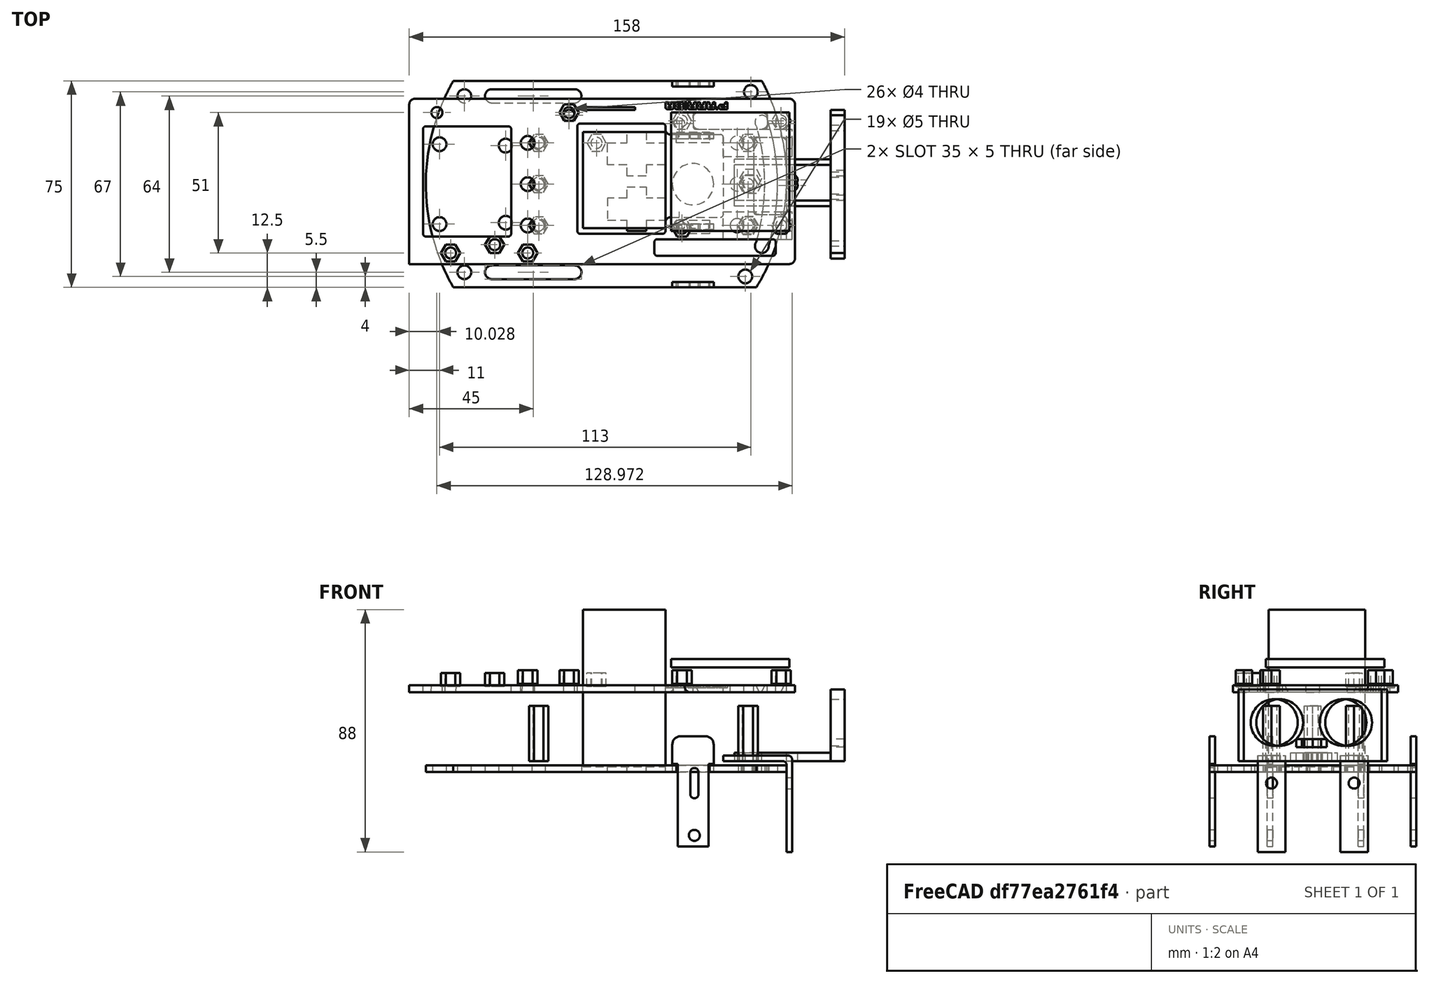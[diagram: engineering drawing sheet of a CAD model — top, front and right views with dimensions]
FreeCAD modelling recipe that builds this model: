
FCSTD DOCUMENT  (FreeCAD 0.17R13541 (Git))
Label: masayloChino2020B
License: All rights reserved
LicenseURL: http://en.wikipedia.org/wiki/All_rights_reserved
objects: Part::Cylinder×48, Part::Cut×40, Part::Box×29, Part::Feature×23, Part::MultiFuse×21, Part::Prism×17, Part::Extrusion×15, Part::Fillet×11, Mesh::Feature×5, Sketcher::SketchObject×1, PartDesign::Pad×1, PartDesign::Body×1, Part::FeaturePython×1
note: 209 computed .brp shape members not serialized (recipe doc carries the construction recipe); baked Part::Feature solids carry a one-line shape summary decoded from their .brp

FEATURE [Sketcher::SketchObject] Sketch
  MapMode = 5
  Support = -> [XY_Plane]
  sketch-geometry (71):
    g0: LineSegment StartX=0 StartY=37.5 StartZ=0 EndX=81 EndY=37.5 EndZ=0
    g1: LineSegment StartX=110 StartY=-37.5 StartZ=0 EndX=93 EndY=-37.5 EndZ=0
    g2: Circle CenterX=4 CenterY=-32 CenterZ=0 NormalX=0 NormalY=0 NormalZ=1 AngleXU=0 Radius=2.5
    g3: ArcOfCircle CenterX=14 CenterY=-32 CenterZ=0 NormalX=0 NormalY=0 NormalZ=1 AngleXU=0 Radius=2.5 StartAngle=1.5708 EndAngle=4.71239
    g4: ArcOfCircle CenterX=44 CenterY=-32 CenterZ=0 NormalX=0 NormalY=0 NormalZ=1 AngleXU=0 Radius=2.5 StartAngle=4.71239 EndAngle=7.85398
    g5: LineSegment StartX=14 StartY=-34.5 StartZ=0 EndX=44 EndY=-34.5 EndZ=0
    g6: LineSegment StartX=14 StartY=-29.5 StartZ=0 EndX=44 EndY=-29.5 EndZ=0
    g7: Circle CenterX=-5 CenterY=-14.5 CenterZ=0 NormalX=0 NormalY=0 NormalZ=1 AngleXU=0 Radius=2.5
    g8: Circle CenterX=-5 CenterY=14.5 CenterZ=0 NormalX=0 NormalY=0 NormalZ=1 AngleXU=0 Radius=2.5
    g9: Circle CenterX=19 CenterY=-14 CenterZ=0 NormalX=0 NormalY=0 NormalZ=1 AngleXU=0 Radius=2.5
    g10: Circle CenterX=31 CenterY=-15 CenterZ=0 NormalX=0 NormalY=0 NormalZ=1 AngleXU=0 Radius=2.5
    g11: ArcOfCircle CenterX=65.3673 CenterY=0 CenterZ=0 NormalX=0 NormalY=0 NormalZ=1 AngleXU=0 Radius=75.36 StartAngle=2.62075 EndAngle=3.66244
    g12: ArcOfCircle CenterX=14 CenterY=32 CenterZ=0 NormalX=0 NormalY=0 NormalZ=1 AngleXU=0 Radius=2.5 StartAngle=1.5708 EndAngle=4.71239
    g13: ArcOfCircle CenterX=44 CenterY=32 CenterZ=0 NormalX=0 NormalY=0 NormalZ=1 AngleXU=0 Radius=2.5 StartAngle=4.71239 EndAngle=7.85398
    g14: LineSegment StartX=14 StartY=29.5 StartZ=0 EndX=44 EndY=29.5 EndZ=0
    g15: LineSegment StartX=14 StartY=34.5 StartZ=0 EndX=44 EndY=34.5 EndZ=0
    g16: Circle CenterX=4 CenterY=32 CenterZ=0 NormalX=0 NormalY=0 NormalZ=1 AngleXU=0 Radius=2.5
    g17: Circle CenterX=31 CenterY=0 CenterZ=0 NormalX=0 NormalY=0 NormalZ=1 AngleXU=0 Radius=2.5
    g18: Circle CenterX=31 CenterY=15 CenterZ=0 NormalX=0 NormalY=0 NormalZ=1 AngleXU=0 Radius=2.5
    g19: LineSegment StartX=56 StartY=-13 StartZ=0 EndX=63 EndY=-13 EndZ=0
    g20: LineSegment StartX=77 StartY=-13 StartZ=0 EndX=77 EndY=-5 EndZ=0
    g21: LineSegment StartX=77 StartY=-5 StartZ=0 EndX=70 EndY=-5 EndZ=0
    g22: LineSegment StartX=56 StartY=-5 StartZ=0 EndX=56 EndY=-13 EndZ=0
    g23: LineSegment StartX=63 StartY=-1 StartZ=0 EndX=70 EndY=-1 EndZ=0
    g24: LineSegment StartX=70 StartY=-1 StartZ=0 EndX=70 EndY=-5 EndZ=0
    g25: LineSegment StartX=70 StartY=-17 StartZ=0 EndX=63 EndY=-17 EndZ=0
    g26: LineSegment StartX=63 StartY=-17 StartZ=0 EndX=63 EndY=-13 EndZ=0
    g27: LineSegment StartX=63 StartY=-5 StartZ=0 EndX=56 EndY=-5 EndZ=0
    g28: LineSegment StartX=63 StartY=-5 StartZ=0 EndX=63 EndY=-1 EndZ=0
    g29: LineSegment StartX=70 StartY=-13 StartZ=0 EndX=70 EndY=-17 EndZ=0
    g30: LineSegment StartX=70 StartY=-13 StartZ=0 EndX=77 EndY=-13 EndZ=0
    g31: Circle CenterX=87 CenterY=0 CenterZ=0 NormalX=0 NormalY=0 NormalZ=1 AngleXU=0 Radius=7.5
    g32: LineSegment StartX=63 StartY=19 StartZ=0 EndX=70 EndY=19 EndZ=0
    g33: LineSegment StartX=70 StartY=19 StartZ=0 EndX=70 EndY=15 EndZ=0
    g34: LineSegment StartX=70 StartY=3 StartZ=0 EndX=63 EndY=3 EndZ=0
    g35: LineSegment StartX=63 StartY=3 StartZ=0 EndX=63 EndY=7 EndZ=0
    g36: LineSegment StartX=56 StartY=15 StartZ=0 EndX=63 EndY=15 EndZ=0
    g37: LineSegment StartX=77 StartY=15 StartZ=0 EndX=77 EndY=7 EndZ=0
    g38: LineSegment StartX=77 StartY=7 StartZ=0 EndX=70 EndY=7 EndZ=0
    g39: LineSegment StartX=56 StartY=7 StartZ=0 EndX=56 EndY=15 EndZ=0
    g40: LineSegment StartX=63 StartY=15 StartZ=0 EndX=63 EndY=19 EndZ=0
    g41: LineSegment StartX=70 StartY=7 StartZ=0 EndX=70 EndY=3 EndZ=0
    g42: LineSegment StartX=63 StartY=7 StartZ=0 EndX=56 EndY=7 EndZ=0
    g43: LineSegment StartX=70 StartY=15 StartZ=0 EndX=77 EndY=15 EndZ=0
    g44: LineSegment StartX=81 StartY=-13 StartZ=0 EndX=93 EndY=-13 EndZ=0
    g45: LineSegment StartX=93 StartY=-13 StartZ=0 EndX=93 EndY=-18 EndZ=0
    g46: LineSegment StartX=93 StartY=-18 StartZ=0 EndX=81 EndY=-18 EndZ=0
    g47: LineSegment StartX=81 StartY=-18 StartZ=0 EndX=81 EndY=-13 EndZ=0
    g48: LineSegment StartX=81 StartY=19 StartZ=0 EndX=93 EndY=19 EndZ=0
    g49: LineSegment StartX=93 StartY=19 StartZ=0 EndX=93 EndY=15 EndZ=0
    g50: LineSegment StartX=93 StartY=15 StartZ=0 EndX=81 EndY=15 EndZ=0
    g51: LineSegment StartX=81 StartY=15 StartZ=0 EndX=81 EndY=19 EndZ=0
    g52: Circle CenterX=107 CenterY=0 CenterZ=0 NormalX=0 NormalY=0 NormalZ=1 AngleXU=0 Radius=2
    g53: Circle CenterX=107 CenterY=-15 CenterZ=0 NormalX=0 NormalY=0 NormalZ=1 AngleXU=0 Radius=2.5
    g54: Circle CenterX=107 CenterY=15 CenterZ=0 NormalX=0 NormalY=0 NormalZ=1 AngleXU=0 Radius=2.5
    g55: Circle CenterX=106 CenterY=-33.5 CenterZ=0 NormalX=0 NormalY=0 NormalZ=1 AngleXU=0 Radius=2.5
    g56: Circle CenterX=108 CenterY=33.5 CenterZ=0 NormalX=0 NormalY=0 NormalZ=1 AngleXU=0 Radius=2.5
    g57: ArcOfCircle CenterX=45.6636 CenterY=1.7423 CenterZ=0 NormalX=0 NormalY=0 NormalZ=1 AngleXU=0 Radius=75.36 StartAngle=5.73548 EndAngle=6.77757
    g58: ArcOfCircle CenterX=112 CenterY=22.5 CenterZ=0 NormalX=0 NormalY=0 NormalZ=1 AngleXU=0 Radius=2.5 StartAngle=0.75994 EndAngle=3.89869
    g59: ArcOfCircle CenterX=112 CenterY=-22.5 CenterZ=0 NormalX=0 NormalY=0 NormalZ=1 AngleXU=0 Radius=2.5 StartAngle=2.5229 EndAngle=6.37272
    g60: ArcOfCircle CenterX=39.6948 CenterY=-0.112448 CenterZ=0 NormalX=0 NormalY=0 NormalZ=1 AngleXU=0 Radius=78.01 StartAngle=5.9951 EndAngle=6.60042
    g61: ArcOfCircle CenterX=38.1627 CenterY=0.243776 CenterZ=0 NormalX=0 NormalY=0 NormalZ=1 AngleXU=0 Radius=74.8917 StartAngle=5.99488 EndAngle=6.561
    g62: LineSegment StartX=81 StartY=-35.5 StartZ=0 EndX=93 EndY=-35.5 EndZ=0
    g63: LineSegment StartX=93 StartY=-35.5 StartZ=0 EndX=93 EndY=-37.5 EndZ=0
    g64: LineSegment StartX=81 StartY=-37.5 StartZ=0 EndX=81 EndY=-35.5 EndZ=0
    g65: LineSegment StartX=81 StartY=-37.5 StartZ=0 EndX=0 EndY=-37.5 EndZ=0
    g66: LineSegment StartX=93 StartY=37.5 StartZ=0 EndX=93 EndY=35.5 EndZ=0
    g67: LineSegment StartX=93 StartY=35.5 StartZ=0 EndX=81 EndY=35.5 EndZ=0
    g68: LineSegment StartX=81 StartY=35.5 StartZ=0 EndX=81 EndY=37.5 EndZ=0
    g69: LineSegment StartX=93 StartY=37.5 StartZ=0 EndX=112 EndY=37.5 EndZ=0
    g70: Circle CenterX=19 CenterY=14 CenterZ=0 NormalX=0 NormalY=0 NormalZ=1 AngleXU=0 Radius=2.5
  constraints (200):
    c: Horizontal(g0)
    c: Horizontal(g1)
    c: DistanceX(g65,g1) = 110
    c: DistanceY(g1,g69) = 75
    c: PointOnObject(g0,g-2)
    c: Radius(g2) = 2.5
    c: DistanceY(g65,g2) = 5.5
    c: DistanceX(g2) = 4
    c: Tangent(g3,g6) = 1.5708
    c: Tangent(g3,g5) = -1.5708
    c: Tangent(g5,g4) = -1.5708
    c: Tangent(g6,g4) = 1.5708
    c: Horizontal(g5)
    c: Equal(g3,g4)
    c: Radius(g3) = 2.5
    c: DistanceY(g65,g3) = 5.5
    c: DistanceX(g3,g4) = 30
    c: DistanceX(g2,g3) = 10
    c: Radius(g7) = 2.5
    c: DistanceY(g65,g7) = 23
    c: DistanceX(g7,g65) = 5
    c: Radius(g8) = 2.5
    c: DistanceY(g8,g0) = 23
    c: DistanceX(g8,g0) = 5
    c: Radius(g9) = 2.5
    c: DistanceY(g2,g9) = 18
    c: DistanceX(g2,g9) = 15
    c: Radius(g10) = 2.5
    c: DistanceX(g9,g10) = 12
    c: DistanceY(g3,g10) = 17
    c: DistanceY(g65,g-1) = 37.5
    c: Coincident(g11,g65)
    c: Radius(g11) = 75.36
    c: Coincident(g11,g0)
    c: PointOnObject(g65,g-2)
    c: Tangent(g12,g15) = 1.5708
    c: Tangent(g12,g14) = -1.5708
    c: Tangent(g14,g13) = -1.5708
    c: Tangent(g15,g13) = 1.5708
    c: Horizontal(g14)
    c: Equal(g12,g13)
    c: Radius(g13) = 2.5
    c: DistanceX(g12,g13) = 30
    c: Radius(g16) = 2.5
    c: DistanceX(g0,g16) = 4
    c: DistanceY(g16,g0) = 5.5
    c: DistanceY(g12,g0) = 5.5
    c: DistanceX(g16,g12) = 10
    c: Radius(g18) = 2.5
    c: Radius(g17) = 2.5
    c: DistanceX(g9,g17) = 12
    c: DistanceY(g10,g17) = 15
    c: DistanceX(g9,g18) = 12
    c: DistanceY(g17,g18) = 15
    c: Coincident(g30,g20)
    c: Coincident(g20,g21)
    c: Coincident(g27,g22)
    c: Coincident(g22,g19)
    c: Horizontal(g19)
    c: Horizontal(g21)
    c: Vertical(g20)
    c: Vertical(g22)
    c: DistanceX(g4,g27) = 12
    c: DistanceX(g27,g20) = 21
    c: DistanceY(g20,g20) = 8
    c: DistanceY(g4,g19) = 19
    c: Coincident(g23,g24)
    c: Coincident(g29,g25)
    c: Coincident(g25,g26)
    c: Coincident(g28,g23)
    c: Horizontal(g23)
    c: Horizontal(g25)
    c: Vertical(g24)
    c: Vertical(g26)
    c: DistanceX(g19,g25) = 7
    c: DistanceY(g25,g19) = 4
    c: DistanceY(g27,g23) = 4
    c: DistanceX(g23,g23) = 7
    c: Tangent(g21,g27)
    c: Coincident(g28,g27)
    c: Tangent(g26,g28)
    c: Coincident(g24,g21)
    c: Tangent(g24,g29)
    c: Coincident(g19,g26)
    c: Coincident(g30,g29)
    c: Tangent(g19,g30)
    c: Radius(g31) = 7.5
    c: PointOnObject(g31,g-1)
    c: DistanceX(g20,g31) = 10
    c: Coincident(g32,g33)
    c: Coincident(g41,g34)
    c: Coincident(g34,g35)
    c: Coincident(g40,g32)
    c: Horizontal(g32)
    c: Horizontal(g34)
    c: Vertical(g33)
    c: Vertical(g35)
    c: Coincident(g43,g37)
    c: Coincident(g37,g38)
    c: Coincident(g42,g39)
    c: Coincident(g39,g36)
    c: Horizontal(g36)
    c: Horizontal(g38)
    c: Vertical(g37)
    c: Vertical(g39)
    c: Tangent(g35,g40)
    c: Tangent(g33,g41)
    c: Coincident(g38,g41)
    c: Coincident(g42,g35)
    c: Tangent(g38,g42)
    c: Coincident(g36,g40)
    c: Coincident(g43,g33)
    c: Tangent(g36,g43)
    c: DistanceX(g42,g42) = 7
    c: DistanceY(g35,g35) = 4
    c: DistanceX(g34,g23) = 0
    c: DistanceY(g23,g34) = 4
    c: DistanceX(g34,g23) = 0
    c: DistanceX(g38,g38) = 7
    c: DistanceY(g37,g37) = 8
    c: DistanceY(g33,g32) = 4
    c: Coincident(g44,g45)
    c: Coincident(g45,g46)
    c: Coincident(g46,g47)
    c: Coincident(g47,g44)
    c: Horizontal(g44)
    c: Horizontal(g46)
    c: Vertical(g45)
    c: Vertical(g47)
    c: DistanceX(g46,g46) = 12
    c: DistanceY(g45,g45) = 5
    c: DistanceX(g20,g44) = 4
    c: DistanceY(g20,g44) = 0
    c: Coincident(g48,g49)
    c: Coincident(g49,g50)
    c: Coincident(g50,g51)
    c: Coincident(g51,g48)
    c: Horizontal(g48)
    c: Horizontal(g50)
    c: Vertical(g49)
    c: Vertical(g51)
    c: DistanceX(g50,g50) = 12
    c: DistanceY(g49,g49) = 4
    c: DistanceY(g37,g50) = 0
    c: DistanceX(g37,g50) = 4
    c: PointOnObject(g52,g-1)
    c: Radius(g52) = 2
    c: DistanceX(g31,g52) = 20
    c: Radius(g53) = 2.5
    c: Radius(g54) = 2.5
    c: DistanceX(g53,g52) = 0
    c: DistanceX(g54,g52) = 0
    c: DistanceY(g52,g54) = 15
    c: DistanceY(g53,g52) = 15
    c: Radius(g55) = 2.5
    c: DistanceX(g55,g1) = 4
    c: DistanceY(g1,g55) = 4
    c: Radius(g56) = 2.5
    c: DistanceX(g56,g69) = 4
    c: DistanceY(g56,g69) = 4
    c: Coincident(g57,g69)
    c: Coincident(g57,g1)
    c: DistanceX(g0,g69) = 112
    c: Radius(g57) = 75.36
    c: Radius(g59) = 2.5
    c: Radius(g58) = 2.5
    c: DistanceY(g54,g58) = 7.5
    c: DistanceX(g54,g58) = 5
    c: DistanceY(g59,g53) = 7.5
    c: DistanceX(g53,g59) = 5
    c: Coincident(g58,g60)
    c: Coincident(g58,g61)
    c: Coincident(g59,g61)
    c: Coincident(g59,g60)
    c: Coincident(g62,g63)
    c: Coincident(g64,g62)
    c: Horizontal(g62)
    c: Vertical(g63)
    c: Vertical(g64)
    c: DistanceX(g62,g46) = 0
    c: DistanceX(g45,g62) = 0
    c: DistanceY(g64,g62) = 2
    c: Coincident(g1,g63)
    c: PointOnObject(g65,g64)
    c: Tangent(g1,g65)
    c: Coincident(g66,g67)
    c: Coincident(g67,g68)
    c: Horizontal(g67)
    c: Vertical(g66)
    c: Vertical(g68)
    c: PointOnObject(g66,g0)
    c: DistanceY(g66,g66) = 2
    c: DistanceX(g48,g66) = 0
    c: DistanceX(g67,g48) = 0
    c: PointOnObject(g0,g68)
    c: PointOnObject(g69,g66)
    c: Tangent(g0,g69)
    c: Radius(g70) = 2.5
    c: DistanceX(g70,g18) = 12
    c: DistanceY(g70,g18) = 1
FEATURE [PartDesign::Pad] Pad
  Length = 2.5
  Length2 = 100
  Profile = -> Sketch
  Type = 0
FEATURE [PartDesign::Body] Body
  Group = -> [Sketch,Pad]
  Origin = -> Origin
  Tip = -> Pad
FEATURE [Part::Box] Box  label="Cubo"
  AttacherType = Attacher::AttachEngine3D
  Height = 2.5
  Length = 140
  Placement = pos=(10,-31,25) rot=(0,0,1;0rad)
  Width = 60
FEATURE [Part::Cylinder] Cylinder  label="Cilindro"
  Angle = 360
  AttacherType = Attacher::AttachEngine3D
  Height = 50
  Placement = pos=(31,0,-4) rot=(0,0,1;0rad)
  Radius = 2.5
FEATURE [Part::Cylinder] Cylinder001  label="Cilindro001"
  Angle = 360
  AttacherType = Attacher::AttachEngine3D
  Height = 50
  Placement = pos=(31,-15,-4) rot=(0,0,1;0rad)
  Radius = 2.5
FEATURE [Part::Cylinder] Cylinder002  label="Cilindro002"
  Angle = 360
  AttacherType = Attacher::AttachEngine3D
  Height = 50
  Placement = pos=(31,15,-4) rot=(0,0,1;0rad)
  Radius = 2.5
FEATURE [Part::Cylinder] Cylinder003  label="Cilindro003"
  Angle = 360
  AttacherType = Attacher::AttachEngine3D
  Height = 50
  Placement = pos=(107,15,-4) rot=(0,0,1;0rad)
  Radius = 2.5
FEATURE [Part::Cylinder] Cylinder004  label="Cilindro004"
  Angle = 360
  AttacherType = Attacher::AttachEngine3D
  Height = 50
  Placement = pos=(107,0,-4) rot=(0,0,1;0rad)
  Radius = 2.5
FEATURE [Part::Cylinder] Cylinder005  label="Cilindro005"
  Angle = 360
  AttacherType = Attacher::AttachEngine3D
  Height = 50
  Placement = pos=(107,-15,-4) rot=(0,0,1;0rad)
  Radius = 2.5
FEATURE [Part::MultiFuse] Fusion
  Shapes = -> [Cylinder,Cylinder001,Cylinder002,Cylinder003,Cylinder004,Cylinder005]
FEATURE [Part::Cut] Cut
  Base = -> Box
  Tool = -> Fusion
FEATURE [Part::Cylinder] Cylinder006  label="Cilindro006"
  Angle = 360
  AttacherType = Attacher::AttachEngine3D
  Height = 10
  Placement = pos=(3,3,47) rot=(0,0,1;0rad)
  Radius = 2
FEATURE [Part::Cylinder] Cylinder007  label="Cilindro007"
  Angle = 360
  AttacherType = Attacher::AttachEngine3D
  Height = 10
  Placement = pos=(3,40,47) rot=(0,0,1;0rad)
  Radius = 2
FEATURE [Part::Cylinder] Cylinder008  label="Cilindro008"
  Angle = 360
  AttacherType = Attacher::AttachEngine3D
  Height = 10
  Placement = pos=(40,3,47) rot=(0,0,1;0rad)
  Radius = 2
FEATURE [Part::Cylinder] Cylinder009  label="Cilindro009"
  Angle = 360
  AttacherType = Attacher::AttachEngine3D
  Height = 10
  Placement = pos=(40,40,47) rot=(0,0,1;0rad)
  Radius = 2
FEATURE [Part::Box] Box001  label="l298n"
  AttacherType = Attacher::AttachEngine3D
  Height = 3
  Length = 43
  Placement = pos=(79,-17,38) rot=(0,0,1;0rad)
  Width = 43
FEATURE [Part::MultiFuse] Fusion001  label="TALADROSL298N"
  Placement = pos=(12,-25,-27) rot=(0,0,1;0rad)
  Shapes = -> [Cylinder006,Cylinder007,Cylinder009,Cylinder008]
FEATURE [Part::Cylinder] Cylinder010  label="Cilindro010"
  Angle = 360
  AttacherType = Attacher::AttachEngine3D
  Height = 10
  Placement = pos=(31,-16,-2) rot=(0,0,1;0rad)
  Radius = 2
FEATURE [Part::Cylinder] Cylinder011  label="Cilindro011"
  Angle = 360
  AttacherType = Attacher::AttachEngine3D
  Height = 10
  Placement = pos=(79,-17,-2) rot=(0,0,1;0rad)
  Radius = 2
FEATURE [Part::Cylinder] Cylinder012  label="Cilindro012"
  Angle = 360
  AttacherType = Attacher::AttachEngine3D
  Height = 10
  Placement = pos=(74,34,-2) rot=(0,0,1;0rad)
  Radius = 2
FEATURE [Part::Cylinder] Cylinder013  label="Cilindro013"
  Angle = 360
  AttacherType = Attacher::AttachEngine3D
  Height = 10
  Placement = pos=(46,34,-2) rot=(0,0,1;0rad)
  Radius = 2
FEATURE [Part::MultiFuse] Fusion002  label="taladrosNanoShield"
  Placement = pos=(61,-9,24) rot=(0,-1,0;0.017453rad)
  Shapes = -> [Cylinder013,Cylinder011,Cylinder010,Cylinder012]
FEATURE [Part::MultiFuse] Fusion003  label="TALADROSPISO2"
  Shapes = -> [Fusion001,Fusion002]
FEATURE [Part::Cut] Cut001
  Base = -> Cut
  Tool = -> Fusion003
FEATURE [Part::Box] Box002  label="Cubo001"
  AttacherType = Attacher::AttachEngine3D
  Height = 10
  Length = 52
  Placement = pos=(36,-18,20) rot=(0,0,1;0rad)
  Width = 30
FEATURE [Part::Box] Box003  label="Cubo002"
  AttacherType = Attacher::AttachEngine3D
  Height = 10
  Length = 19
  Placement = pos=(68,-28,20) rot=(0,0,1;0rad)
  Width = 1
FEATURE [Part::Box] Box004  label="Cubo003"
  AttacherType = Attacher::AttachEngine3D
  Height = 10
  Length = 12
  Placement = pos=(13,-17,20) rot=(0,0,1;0rad)
  Width = 28
FEATURE [Part::Box] Box005  label="Cubo004"
  AttacherType = Attacher::AttachEngine3D
  Height = 10
  Length = 44
  Placement = pos=(17,20,20) rot=(0,0,1;0rad)
  Width = 6
FEATURE [Part::Box] Box006  label="Cubo005"
  AttacherType = Attacher::AttachEngine3D
  Height = 10
  Length = 27
  Placement = pos=(20,-26,20) rot=(0,0,1;0rad)
  Width = 6
FEATURE [Part::MultiFuse] Fusion004  label="agujerosPiso2"
  Shapes = -> [Box002,Box003,Box004,Box005,Box006]
FEATURE [Part::Cut] Cut002
  Base = -> Cut001
  Tool = -> Fusion004
FEATURE [Part::Fillet] Fillet  label="piso2"
  Base = -> Cut002
  Edges = 4 edges r=2: [Edge1,Edge3,Edge6,Edge47]
  Placement = pos=(0,0,4) rot=(0,0,1;0rad)
FEATURE [Part::Cylinder] Cylinder014  label="Cilindro014"
  Angle = 360
  AttacherType = Attacher::AttachEngine3D
  Height = 30
  Placement = pos=(0,0,-2) rot=(0,0,1;0rad)
  Radius = 2
FEATURE [Part::Prism] Prism  label="Prisma"
  AttacherType = Attacher::AttachEngine3D
  Circumradius = 3.5
  Height = 20
  Polygon = 6
FEATURE [Part::Cut] Cut003  label="separador"
  Base = -> Prism
  Placement = pos=(31,0,4) rot=(0,0,1;0rad)
  Tool = -> Cylinder014
FEATURE [Part::Cylinder] Cylinder015  label="Cilindro015"
  Angle = 360
  AttacherType = Attacher::AttachEngine3D
  Height = 30
  Placement = pos=(0,0,-2) rot=(0,0,1;0rad)
  Radius = 2
FEATURE [Part::Prism] Prism001  label="Prisma001"
  AttacherType = Attacher::AttachEngine3D
  Circumradius = 3.5
  Height = 20
  Polygon = 6
FEATURE [Part::Cut] Cut004  label="separador001"
  Base = -> Prism001
  Placement = pos=(31,15,4) rot=(0,0,1;0rad)
  Tool = -> Cylinder015
FEATURE [Part::Cylinder] Cylinder016  label="Cilindro016"
  Angle = 360
  AttacherType = Attacher::AttachEngine3D
  Height = 30
  Placement = pos=(0,0,-2) rot=(0,0,1;0rad)
  Radius = 2
FEATURE [Part::Prism] Prism002  label="Prisma002"
  AttacherType = Attacher::AttachEngine3D
  Circumradius = 3.5
  Height = 20
  Polygon = 6
FEATURE [Part::Cut] Cut005  label="separador002"
  Base = -> Prism002
  Placement = pos=(31,-15,4) rot=(0,0,1;0rad)
  Tool = -> Cylinder016
FEATURE [Part::Prism] Prism003  label="Prisma003"
  AttacherType = Attacher::AttachEngine3D
  Circumradius = 3.5
  Height = 20
  Polygon = 6
FEATURE [Part::Cylinder] Cylinder017  label="Cilindro017"
  Angle = 360
  AttacherType = Attacher::AttachEngine3D
  Height = 30
  Placement = pos=(0,0,-2) rot=(0,0,1;0rad)
  Radius = 2
FEATURE [Part::Cut] Cut006  label="separador003"
  Base = -> Prism003
  Placement = pos=(107,-15,4) rot=(0,0,1;0rad)
  Tool = -> Cylinder017
FEATURE [Part::Cylinder] Cylinder018  label="Cilindro018"
  Angle = 360
  AttacherType = Attacher::AttachEngine3D
  Height = 30
  Placement = pos=(0,0,-2) rot=(0,0,1;0rad)
  Radius = 2
FEATURE [Part::Prism] Prism004  label="Prisma004"
  AttacherType = Attacher::AttachEngine3D
  Circumradius = 3.5
  Height = 20
  Polygon = 6
FEATURE [Part::Cut] Cut007  label="separador004"
  Base = -> Prism004
  Placement = pos=(107,0,4) rot=(0,0,1;0rad)
  Tool = -> Cylinder018
FEATURE [Part::Cylinder] Cylinder019  label="Cilindro019"
  Angle = 360
  AttacherType = Attacher::AttachEngine3D
  Height = 30
  Placement = pos=(0,0,-2) rot=(0,0,1;0rad)
  Radius = 2
FEATURE [Part::Prism] Prism005  label="Prisma005"
  AttacherType = Attacher::AttachEngine3D
  Circumradius = 3.5
  Height = 20
  Polygon = 6
FEATURE [Part::Cut] Cut008  label="separador005"
  Base = -> Prism005
  Placement = pos=(107,15,4) rot=(0,0,1;0rad)
  Tool = -> Cylinder019
FEATURE [Part::Box] Box007  label="Cubo006"
  AttacherType = Attacher::AttachEngine3D
  Height = 33
  Length = 11.2
  Placement = pos=(81.5,35.5,-27) rot=(0,0,1;0rad)
  Width = 2
FEATURE [Part::Cylinder] Cylinder022  label="Cilindro022"
  Angle = 360
  AttacherType = Attacher::AttachEngine3D
  Height = 10
  Placement = pos=(87.5,41.5,-8) rot=(1,0,0;1.5708rad)
  Radius = 1.5
FEATURE [Part::Box] Box009  label="Cubo008"
  AttacherType = Attacher::AttachEngine3D
  Height = 8
  Length = 3
  Placement = pos=(86,32,-8) rot=(0,0,1;0rad)
  Width = 10
FEATURE [Part::Cylinder] Cylinder021  label="Cilindro021"
  Angle = 360
  AttacherType = Attacher::AttachEngine3D
  Height = 10
  Placement = pos=(87.5,41.5,0) rot=(1,0,0;1.5708rad)
  Radius = 1.5
FEATURE [Part::Cylinder] Cylinder023  label="Cilindro023"
  Angle = 360
  AttacherType = Attacher::AttachEngine3D
  Height = 10
  Placement = pos=(87.5,41.5,-23) rot=(1,0,0;1.5708rad)
  Radius = 2
FEATURE [Part::MultiFuse] Fusion006
  Shapes = -> [Box009,Cylinder022,Cylinder021,Cylinder023]
FEATURE [Part::Box] Box008  label="Cubo007"
  AttacherType = Attacher::AttachEngine3D
  Height = 10
  Length = 15
  Placement = pos=(79.5,35.5,3) rot=(0,0,1;0rad)
  Width = 2
FEATURE [Part::MultiFuse] Fusion005
  Shapes = -> [Box007,Box008]
FEATURE [Part::Fillet] Fillet001
  Base = -> Fusion005
  Edges = 2 edges r=3: [Edge30,Edge32]
FEATURE [Part::Cut] Cut010  label="colocador"
  Base = -> Fillet001
  Tool = -> Fusion006
FEATURE [Part::Box] Box010  label="Cubo009"
  AttacherType = Attacher::AttachEngine3D
  Height = 33
  Length = 11.2
  Placement = pos=(81.5,35.5,-27) rot=(0,0,1;0rad)
  Width = 2
FEATURE [Part::Cylinder] Cylinder024  label="Cilindro024"
  Angle = 360
  AttacherType = Attacher::AttachEngine3D
  Height = 10
  Placement = pos=(87.5,41.5,0) rot=(1,0,0;1.5708rad)
  Radius = 1.5
FEATURE [Part::Box] Box011  label="Cubo010"
  AttacherType = Attacher::AttachEngine3D
  Height = 10
  Length = 15
  Placement = pos=(79.5,35.5,3) rot=(0,0,1;0rad)
  Width = 2
FEATURE [Part::MultiFuse] Fusion007
  Shapes = -> [Box010,Box011]
FEATURE [Part::Fillet] Fillet002
  Base = -> Fusion007
  Edges = 2 edges r=3: [Edge30,Edge32]
FEATURE [Part::Cylinder] Cylinder025  label="Cilindro025"
  Angle = 360
  AttacherType = Attacher::AttachEngine3D
  Height = 10
  Placement = pos=(87.5,41.5,-8) rot=(1,0,0;1.5708rad)
  Radius = 1.5
FEATURE [Part::Cylinder] Cylinder026  label="Cilindro026"
  Angle = 360
  AttacherType = Attacher::AttachEngine3D
  Height = 10
  Placement = pos=(87.5,41.5,-23) rot=(1,0,0;1.5708rad)
  Radius = 2
FEATURE [Part::Box] Box012  label="Cubo011"
  AttacherType = Attacher::AttachEngine3D
  Height = 8
  Length = 3
  Placement = pos=(86,32,-8) rot=(0,0,1;0rad)
  Width = 10
FEATURE [Part::MultiFuse] Fusion008
  Shapes = -> [Box012,Cylinder025,Cylinder024,Cylinder026]
FEATURE [Part::Cut] Cut011  label="colocador001"
  Base = -> Fillet002
  Placement = pos=(0,-19,0) rot=(0,0,1;0rad)
  Tool = -> Fusion008
FEATURE [Part::Box] Box013  label="Cubo012"
  AttacherType = Attacher::AttachEngine3D
  Height = 33
  Length = 11.2
  Placement = pos=(81.5,35.5,-27) rot=(0,0,1;0rad)
  Width = 2
FEATURE [Part::Cylinder] Cylinder027  label="Cilindro027"
  Angle = 360
  AttacherType = Attacher::AttachEngine3D
  Height = 10
  Placement = pos=(87.5,41.5,0) rot=(1,0,0;1.5708rad)
  Radius = 1.5
FEATURE [Part::Box] Box014  label="Cubo013"
  AttacherType = Attacher::AttachEngine3D
  Height = 10
  Length = 15
  Placement = pos=(79.5,35.5,3) rot=(0,0,1;0rad)
  Width = 2
FEATURE [Part::MultiFuse] Fusion009
  Shapes = -> [Box013,Box014]
FEATURE [Part::Fillet] Fillet003
  Base = -> Fusion009
  Edges = 2 edges r=3: [Edge30,Edge32]
FEATURE [Part::Cylinder] Cylinder028  label="Cilindro028"
  Angle = 360
  AttacherType = Attacher::AttachEngine3D
  Height = 10
  Placement = pos=(87.5,41.5,-8) rot=(1,0,0;1.5708rad)
  Radius = 1.5
FEATURE [Part::Cylinder] Cylinder029  label="Cilindro029"
  Angle = 360
  AttacherType = Attacher::AttachEngine3D
  Height = 10
  Placement = pos=(87.5,41.5,-23) rot=(1,0,0;1.5708rad)
  Radius = 2
FEATURE [Part::Box] Box015  label="Cubo014"
  AttacherType = Attacher::AttachEngine3D
  Height = 8
  Length = 3
  Placement = pos=(86,32,-8) rot=(0,0,1;0rad)
  Width = 10
FEATURE [Part::MultiFuse] Fusion010
  Shapes = -> [Box015,Cylinder028,Cylinder027,Cylinder029]
FEATURE [Part::Cut] Cut012  label="colocador002"
  Base = -> Fillet003
  Placement = pos=(0,-52,0) rot=(0,0,1;0rad)
  Tool = -> Fusion010
FEATURE [Part::Cylinder] Cylinder030  label="Cilindro030"
  Angle = 360
  AttacherType = Attacher::AttachEngine3D
  Height = 10
  Placement = pos=(87.5,41.5,-8) rot=(1,0,0;1.5708rad)
  Radius = 1.5
FEATURE [Part::Box] Box016  label="Cubo015"
  AttacherType = Attacher::AttachEngine3D
  Height = 8
  Length = 3
  Placement = pos=(86,32,-8) rot=(0,0,1;0rad)
  Width = 10
FEATURE [Part::Box] Box017  label="Cubo016"
  AttacherType = Attacher::AttachEngine3D
  Height = 33
  Length = 11.2
  Placement = pos=(81.5,35.5,-27) rot=(0,0,1;0rad)
  Width = 2
FEATURE [Part::Box] Box018  label="Cubo017"
  AttacherType = Attacher::AttachEngine3D
  Height = 10
  Length = 15
  Placement = pos=(79.5,35.5,3) rot=(0,0,1;0rad)
  Width = 2
FEATURE [Part::Cylinder] Cylinder031  label="Cilindro031"
  Angle = 360
  AttacherType = Attacher::AttachEngine3D
  Height = 10
  Placement = pos=(87.5,41.5,-23) rot=(1,0,0;1.5708rad)
  Radius = 2
FEATURE [Part::Cylinder] Cylinder032  label="Cilindro032"
  Angle = 360
  AttacherType = Attacher::AttachEngine3D
  Height = 10
  Placement = pos=(87.5,41.5,0) rot=(1,0,0;1.5708rad)
  Radius = 1.5
FEATURE [Part::MultiFuse] Fusion011
  Shapes = -> [Box017,Box018]
FEATURE [Part::Fillet] Fillet004
  Base = -> Fusion011
  Edges = 2 edges r=3: [Edge30,Edge32]
FEATURE [Part::MultiFuse] Fusion012
  Shapes = -> [Box016,Cylinder030,Cylinder032,Cylinder031]
FEATURE [Part::Cut] Cut013  label="colocador003"
  Base = -> Fillet004
  Placement = pos=(0,-73,0) rot=(0,0,1;0rad)
  Tool = -> Fusion012
FEATURE [Part::Feature] Cut010_solid  label="colocador (Solid)"
  shape: bbox 15 x 2 x 40 mm, 21 faces (baked)
FEATURE [Mesh::Feature] Mesh002  label="colocador (Solid) (Meshed)"
FEATURE [Part::Cylinder] Cylinder033  label="Cilindro033"
  Angle = 360
  AttacherType = Attacher::AttachEngine3D
  Height = 30
  Placement = pos=(0,0,-2) rot=(0,0,1;0rad)
  Radius = 2
FEATURE [Part::Prism] Prism007  label="Prisma007"
  AttacherType = Attacher::AttachEngine3D
  Circumradius = 3.5
  Height = 5
  Polygon = 6
FEATURE [Part::Cylinder] Cylinder034  label="Cilindro034"
  Angle = 360
  AttacherType = Attacher::AttachEngine3D
  Height = 30
  Placement = pos=(0,0,-2) rot=(0,0,1;0rad)
  Radius = 2
FEATURE [Part::Prism] Prism008  label="Prisma008"
  AttacherType = Attacher::AttachEngine3D
  Circumradius = 3.5
  Height = 5
  Polygon = 6
FEATURE [Part::Cut] Cut015  label="separador008"
  Base = -> Prism008
  Placement = pos=(27,-25,32) rot=(0,0,1;0rad)
  Tool = -> Cylinder034
FEATURE [Part::Cylinder] Cylinder035  label="Cilindro035"
  Angle = 360
  AttacherType = Attacher::AttachEngine3D
  Height = 30
  Placement = pos=(0,0,-2) rot=(0,0,1;0rad)
  Radius = 2
FEATURE [Part::Prism] Prism009  label="Prisma009"
  AttacherType = Attacher::AttachEngine3D
  Circumradius = 3.5
  Height = 5
  Polygon = 6
FEATURE [Part::Cut] Cut016  label="separador009"
  Base = -> Prism009
  Placement = pos=(42,26,32) rot=(0,0,1;0rad)
  Tool = -> Cylinder035
FEATURE [Part::Prism] Prism010  label="Prisma010"
  AttacherType = Attacher::AttachEngine3D
  Circumradius = 3.5
  Height = 5
  Polygon = 6
FEATURE [Part::Cylinder] Cylinder036  label="Cilindro036"
  Angle = 360
  AttacherType = Attacher::AttachEngine3D
  Height = 30
  Placement = pos=(0,0,-2) rot=(0,0,1;0rad)
  Radius = 2
FEATURE [Part::Cut] Cut017  label="separador010"
  Base = -> Prism010
  Placement = pos=(119,23,32) rot=(0,0,1;0rad)
  Tool = -> Cylinder036
FEATURE [Part::Prism] Prism011  label="Prisma011"
  AttacherType = Attacher::AttachEngine3D
  Circumradius = 3.5
  Height = 5
  Polygon = 6
FEATURE [Part::Cylinder] Cylinder037  label="Cilindro037"
  Angle = 360
  AttacherType = Attacher::AttachEngine3D
  Height = 30
  Placement = pos=(0,0,-2) rot=(0,0,1;0rad)
  Radius = 2
FEATURE [Part::Cut] Cut018  label="separador011"
  Base = -> Prism011
  Placement = pos=(83,23,32) rot=(0,0,1;0rad)
  Tool = -> Cylinder037
FEATURE [Part::Prism] Prism012  label="Prisma012"
  AttacherType = Attacher::AttachEngine3D
  Circumradius = 3.5
  Height = 5
  Polygon = 6
FEATURE [Part::Cylinder] Cylinder038  label="Cilindro038"
  Angle = 360
  AttacherType = Attacher::AttachEngine3D
  Height = 30
  Placement = pos=(0,0,-2) rot=(0,0,1;0rad)
  Radius = 2
FEATURE [Part::Cut] Cut019  label="separador012"
  Base = -> Prism012
  Placement = pos=(52,15,31) rot=(0,0,1;0rad)
  Tool = -> Cylinder038
FEATURE [Part::Cylinder] Cylinder039  label="Cilindro039"
  Angle = 360
  AttacherType = Attacher::AttachEngine3D
  Height = 30
  Placement = pos=(0,0,-2) rot=(0,0,1;0rad)
  Radius = 2
FEATURE [Part::Prism] Prism013  label="Prisma013"
  AttacherType = Attacher::AttachEngine3D
  Circumradius = 3.5
  Height = 5
  Polygon = 6
FEATURE [Part::Cut] Cut020  label="separador013"
  Base = -> Prism013
  Placement = pos=(119,-15,32) rot=(0,0,1;0rad)
  Tool = -> Cylinder039
FEATURE [Part::Prism] Prism014  label="Prisma014"
  AttacherType = Attacher::AttachEngine3D
  Circumradius = 3.5
  Height = 5
  Polygon = 6
FEATURE [Part::Cylinder] Cylinder040  label="Cilindro040"
  Angle = 360
  AttacherType = Attacher::AttachEngine3D
  Height = 30
  Placement = pos=(0,0,-2) rot=(0,0,1;0rad)
  Radius = 2
FEATURE [Part::Cut] Cut021  label="separador014"
  Base = -> Prism014
  Placement = pos=(83,-16,32) rot=(0,0,1;0rad)
  Tool = -> Cylinder040
FEATURE [Part::Feature] Cut021_solid  label="separadorSec"
  shape: bbox 7 x 6.062 x 5 mm, 9 faces (baked)
FEATURE [Part::Feature] path4522
  shape: bbox 6.314 x 4.985 x 2.279e-07 mm, 0 faces, 0 solids (baked)
FEATURE [Part::Feature] path4522001
  shape: bbox 2.322 x 1.012 x 2.279e-07 mm, 0 faces, 0 solids (baked)
FEATURE [Part::Feature] path4524
  shape: bbox 1.403 x 1.446 x 2.279e-07 mm, 0 faces, 0 solids (baked)
FEATURE [Part::Feature] path4526
  shape: bbox 6.076 x 4.985 x 2.279e-07 mm, 0 faces, 0 solids (baked)
FEATURE [Part::Feature] path4526001
  shape: bbox 2.174 x 0.6621 x 2.279e-07 mm, 0 faces, 0 solids (baked)
FEATURE [Part::Feature] path4528
  shape: bbox 6.274 x 4.977 x 2.279e-07 mm, 0 faces, 0 solids (baked)
FEATURE [Part::Feature] path4528001
  shape: bbox 2.371 x 0.6621 x 2.279e-07 mm, 0 faces, 0 solids (baked)
FEATURE [Part::Feature] path4530
  shape: bbox 6.274 x 4.977 x 2.279e-07 mm, 0 faces, 0 solids (baked)
FEATURE [Part::Feature] path4530001
  shape: bbox 2.371 x 0.6621 x 2.279e-07 mm, 0 faces, 0 solids (baked)
FEATURE [Part::Feature] path4532
  shape: bbox 1.956 x 4.977 x 2.279e-07 mm, 0 faces, 0 solids (baked)
FEATURE [Part::Feature] path4534
  shape: bbox 6.373 x 4.992 x 2.279e-07 mm, 0 faces, 0 solids (baked)
FEATURE [Part::Feature] path4534001
  shape: bbox 2.391 x 0.6849 x 2.279e-07 mm, 0 faces, 0 solids (baked)
FEATURE [Part::Feature] path4534002
  shape: bbox 2.391 x 0.6849 x 2.279e-07 mm, 0 faces, 0 solids (baked)
FEATURE [Part::Feature] path4536
  shape: bbox 6.076 x 4.985 x 2.279e-07 mm, 0 faces, 0 solids (baked)
FEATURE [Part::Feature] path4536001
  shape: bbox 2.174 x 0.6621 x 2.279e-07 mm, 0 faces, 0 solids (baked)
FEATURE [Part::Extrusion] Extrude
  Base = -> path4522
  Dir = (0,0,-1)
  DirMode = 2
  FaceMakerClass = Part::FaceMakerBullseye
  LengthFwd = 2
  LengthRev = 0
  Solid = true
  Symmetric = false
FEATURE [Part::Extrusion] Extrude001
  Base = -> path4522001
  Dir = (0,0,1)
  DirMode = 2
  FaceMakerClass = Part::FaceMakerBullseye
  LengthFwd = 2
  LengthRev = 0
  Placement = pos=(0,0,-2) rot=(0,0,1;0rad)
  Solid = true
  Symmetric = false
FEATURE [Part::Extrusion] Extrude002
  Base = -> path4524
  Dir = (0,0,-1)
  DirMode = 2
  FaceMakerClass = Part::FaceMakerBullseye
  LengthFwd = 2
  LengthRev = 0
  Solid = true
  Symmetric = false
FEATURE [Part::Extrusion] Extrude003
  Base = -> path4526
  Dir = (0,0,-1)
  DirMode = 2
  FaceMakerClass = Part::FaceMakerBullseye
  LengthFwd = 2
  LengthRev = 0
  Solid = true
  Symmetric = false
FEATURE [Part::Extrusion] Extrude004
  Base = -> path4526001
  Dir = (0,0,1)
  DirMode = 2
  FaceMakerClass = Part::FaceMakerBullseye
  LengthFwd = 2
  LengthRev = 0
  Placement = pos=(0,0,-2) rot=(0,0,1;0rad)
  Solid = true
  Symmetric = false
FEATURE [Part::Extrusion] Extrude005
  Base = -> path4528
  Dir = (0,0,-1)
  DirMode = 2
  FaceMakerClass = Part::FaceMakerBullseye
  LengthFwd = 2
  LengthRev = 0
  Solid = true
  Symmetric = false
FEATURE [Part::Extrusion] Extrude006
  Base = -> path4528001
  Dir = (0,0,1)
  DirMode = 2
  FaceMakerClass = Part::FaceMakerBullseye
  LengthFwd = 2
  LengthRev = 0
  Placement = pos=(0,0,-2) rot=(0,0,1;0rad)
  Solid = true
  Symmetric = false
FEATURE [Part::Extrusion] Extrude007
  Base = -> path4530
  Dir = (0,0,-1)
  DirMode = 2
  FaceMakerClass = Part::FaceMakerBullseye
  LengthFwd = 2
  LengthRev = 0
  Solid = true
  Symmetric = false
FEATURE [Part::Extrusion] Extrude008
  Base = -> path4530001
  Dir = (0,0,1)
  DirMode = 2
  FaceMakerClass = Part::FaceMakerBullseye
  LengthFwd = 2
  LengthRev = 0
  Placement = pos=(0,0,-2) rot=(0,0,1;0rad)
  Solid = true
  Symmetric = false
FEATURE [Part::Extrusion] Extrude009
  Base = -> path4532
  Dir = (0,0,-1)
  DirMode = 2
  FaceMakerClass = Part::FaceMakerBullseye
  LengthFwd = 2
  LengthRev = 0
  Solid = true
  Symmetric = false
FEATURE [Part::Extrusion] Extrude010
  Base = -> path4534
  Dir = (0,0,-1)
  DirMode = 2
  FaceMakerClass = Part::FaceMakerBullseye
  LengthFwd = 2
  LengthRev = 0
  Solid = true
  Symmetric = false
FEATURE [Part::Extrusion] Extrude011
  Base = -> path4534001
  Dir = (0,0,1)
  DirMode = 2
  FaceMakerClass = Part::FaceMakerBullseye
  LengthFwd = 2
  LengthRev = 0
  Placement = pos=(0,0,-2) rot=(0,0,1;0rad)
  Solid = true
  Symmetric = false
FEATURE [Part::Extrusion] Extrude012
  Base = -> path4534002
  Dir = (0,0,1)
  DirMode = 2
  FaceMakerClass = Part::FaceMakerBullseye
  LengthFwd = 2
  LengthRev = 0
  Placement = pos=(0,0,-2) rot=(0,0,1;0rad)
  Solid = true
  Symmetric = false
FEATURE [Part::Extrusion] Extrude013
  Base = -> path4536
  Dir = (0,0,-1)
  DirMode = 2
  FaceMakerClass = Part::FaceMakerBullseye
  LengthFwd = 2
  LengthRev = 0
  Solid = true
  Symmetric = false
FEATURE [Part::Extrusion] Extrude014
  Base = -> path4536001
  Dir = (0,0,1)
  DirMode = 2
  FaceMakerClass = Part::FaceMakerBullseye
  LengthFwd = 2
  LengthRev = 0
  Placement = pos=(0,0,-2) rot=(0,0,1;0rad)
  Solid = true
  Symmetric = false
FEATURE [Part::Cut] Cut023
  Base = -> Extrude
  Tool = -> Extrude001
FEATURE [Part::Cut] Cut024
  Base = -> Extrude003
  Tool = -> Extrude004
FEATURE [Part::Cut] Cut025
  Base = -> Extrude005
  Tool = -> Extrude006
FEATURE [Part::Cut] Cut026
  Base = -> Extrude007
  Tool = -> Extrude008
FEATURE [Part::MultiFuse] Fusion014
  Shapes = -> [Extrude011,Extrude012]
FEATURE [Part::Cut] Cut027
  Base = -> Extrude010
  Tool = -> Fusion014
FEATURE [Part::Cut] Cut028
  Base = -> Extrude013
  Tool = -> Extrude014
FEATURE [Part::MultiFuse] Fusion015  label="PARRIBA"
  Placement = pos=(0,43,33) rot=(0,0,1;0rad)
  Shapes = -> [Extrude002,Extrude009,Cut023,Cut024,Cut025,Cut026,Cut027,Cut028]
FEATURE [Part::FeaturePython] Scale  # Draft clone (typed FeaturePython)
  Fuse = false
  Objects = -> [Fusion015]
  Placement = pos=(9.32,6.53,31.7) rot=(0,0,1;0rad)
  Scale = (0.5,0.5,0.5)
FEATURE [Part::Box] Box019  label="portaPilasAA"
  AttacherType = Attacher::AttachEngine3D
  Height = 57
  Length = 30
  Placement = pos=(47,-16,2) rot=(0,0,1;0rad)
  Width = 35
FEATURE [Part::Box] Box020  label="Cubo018"
  AttacherType = Attacher::AttachEngine3D
  Height = 30
  Length = 32
  Placement = pos=(57,-22,12) rot=(0,0,1;0rad)
  Width = 40
FEATURE [Part::Cut] Cut029
  Base = -> Fillet
  Tool = -> Box020
FEATURE [Part::Cut] Cut030
  Base = -> Cut029
  Tool = -> Scale
FEATURE [Part::Box] Box021  label="Cubo019"
  AttacherType = Attacher::AttachEngine3D
  Height = 10
  Length = 32
  Placement = pos=(113,-21,24) rot=(0,0,1;0rad)
  Width = 40
FEATURE [Part::Cut] Cut031
  Base = -> Cut030
  Tool = -> Box021
FEATURE [Part::Fillet] Fillet005
  Base = -> Cut031
  Edges = 8 edges: [Edge485 r1=2 r2=1,Edge486 r1=2 r2=1,Edge487 r1=2 r2=1,Edge488 r1=2 r2=1,Edge489 r1=2 r2=1,Edge490 r1=2 r2=1,Edge491 r1=2 r2=1,Edge492 r1=2 r2=1]
FEATURE [Part::Fillet] Fillet006
  Base = -> Fillet005
  Edges = 4 edges r=1: [Edge495,Edge496,Edge498,Edge500]
FEATURE [Part::Fillet] Fillet007
  Base = -> Fillet006
  Edges = 4 edges r=1: [Edge497,Edge498,Edge500,Edge502]
FEATURE [Part::Fillet] Fillet008
  Base = -> Fillet007
  Edges = 6 edges r=1: [Edge495,Edge498,Edge500,Edge502,Edge504,Edge506]
FEATURE [Part::Fillet] Fillet009  label="segundoPiso"
  Base = -> Fillet008
  Edges = 2 edges r=2: [Edge190,Edge210]
  Placement = pos=(134,0,0) rot=(0,0,1;3.14159rad)
FEATURE [Part::Feature] Cut003_solid  label="separador (Solid)"
  shape: bbox 7 x 6.062 x 20 mm, 9 faces (baked)
FEATURE [Mesh::Feature] Mesh  label="separador (Solid) (Meshed)"
FEATURE [Part::Feature] Fillet009_solid  label="segundoPiso (Solid)"
  shape: bbox 140 x 60 x 3.573 mm, 236 faces (baked)
FEATURE [Mesh::Feature] Mesh003  label="segundoPiso (Solid) (Meshed)"
FEATURE [Part::Box] Box022  label="Cubo020"
  AttacherType = Attacher::AttachEngine3D
  Height = 3
  Length = 9
  Placement = pos=(16,-2,1) rot=(0,0,1;0rad)
  Width = 9
FEATURE [Part::Box] Box023  label="Cubo021"
  AttacherType = Attacher::AttachEngine3D
  Height = 10
  Length = 20
  Placement = pos=(29,5,-5) rot=(0,0,1;0rad)
  Width = 37
FEATURE [Part::Cylinder] Cylinder041  label="Cilindro041"
  Angle = 360
  AttacherType = Attacher::AttachEngine3D
  Height = 10
  Placement = pos=(21.5,34,-9) rot=(0,0,1;0rad)
  Radius = 2
FEATURE [Part::Box] Box024  label="Cubo022"
  AttacherType = Attacher::AttachEngine3D
  Height = 10
  Length = 20
  Placement = pos=(-6,5,-5) rot=(0,0,1;0rad)
  Width = 37
FEATURE [Part::MultiFuse] Fusion017
  Shapes = -> [Box024,Box023]
FEATURE [Part::Box] Box025  label="Cubo023"
  AttacherType = Attacher::AttachEngine3D
  Height = 26
  Length = 52
  Placement = pos=(-5,0,-4) rot=(0,0,1;0rad)
  Width = 5
FEATURE [Part::Box] Box026  label="Cubo024"
  AttacherType = Attacher::AttachEngine3D
  Height = 3
  Length = 52
  Placement = pos=(-5,0,-4) rot=(0,0,1;0rad)
  Width = 40
FEATURE [Part::MultiFuse] Fusion018
  Shapes = -> [Box025,Box026]
FEATURE [Part::Cylinder] Cylinder042  label="Cilindro042"
  Angle = 360
  AttacherType = Attacher::AttachEngine3D
  Height = 10
  Placement = pos=(8,6,10) rot=(1,0,0;1.5708rad)
  Radius = 8.5
FEATURE [Part::Cylinder] Cylinder043  label="Cilindro043"
  Angle = 360
  AttacherType = Attacher::AttachEngine3D
  Height = 10
  Placement = pos=(33,6,10) rot=(1,0,0;1.5708rad)
  Radius = 8.5
FEATURE [Part::MultiFuse] Fusion019
  Shapes = -> [Cylinder042,Cylinder043]
FEATURE [Part::MultiFuse] Fusion016
  Shapes = -> [Box022,Fusion019]
FEATURE [Part::Cut] Cut032
  Base = -> Fusion018
  Tool = -> Fusion016
FEATURE [Part::Cut] Cut034
  Base = -> Cut032
  Tool = -> Cylinder041
FEATURE [Part::Cut] Cut035
  Base = -> Cut034
  Tool = -> Fusion017
FEATURE [Part::Cylinder] Cylinder044  label="Cilindro044"
  Angle = 360
  AttacherType = Attacher::AttachEngine3D
  Height = 10
  Placement = pos=(21.5,19,-9) rot=(0,0,1;0rad)
  Radius = 2
FEATURE [Part::Cut] Cut033
  Base = -> Cut035
  Placement = pos=(184,-18,8) rot=(0,0,1;1.5708rad)
  Tool = -> Cylinder044
FEATURE [Part::Prism] Prism015  label="Prisma015"
  AttacherType = Attacher::AttachEngine3D
  Circumradius = 4
  Height = 12
  Placement = pos=(150,4,0) rot=(0,0,1;0rad)
  Polygon = 6
FEATURE [Part::Cut] Cut036  label="SOPORTEUS"
  Base = -> Cut033
  Placement = pos=(-42,-4,0) rot=(0,0,1;0rad)
  Tool = -> Prism015
FEATURE [Part::Feature] Cut036_solid  label="SOPORTEUS (Solid)"
  shape: bbox 40 x 52 x 26 mm, 27 faces (baked)
FEATURE [Mesh::Feature] Mesh004  label="SOPORTEUS (Solid) (Meshed)"
FEATURE [Part::Cylinder] Cylinder045  label="Cilindro045"
  Angle = 360
  AttacherType = Attacher::AttachEngine3D
  Height = 10
  Placement = pos=(22,5,-3) rot=(0,0,1;0rad)
  Radius = 2
FEATURE [Part::Cylinder] Cylinder046  label="Cilindro046"
  Angle = 360
  AttacherType = Attacher::AttachEngine3D
  Height = 10
  Placement = pos=(-2,5,25) rot=(0,1,0;1.5708rad)
  Radius = 2
FEATURE [Part::Box] Box027  label="Cubo025"
  AttacherType = Attacher::AttachEngine3D
  Height = 35
  Length = 2
  Width = 10
FEATURE [Part::Cylinder] Cylinder047  label="Cilindro047"
  Angle = 360
  AttacherType = Attacher::AttachEngine3D
  Height = 10
  Placement = pos=(-14,7.5,29) rot=(0,0,1;0rad)
  Radius = 2
FEATURE [Part::MultiFuse] Fusion021
  Placement = pos=(0,-2.5,0) rot=(0,0,1;0rad)
  Shapes = -> [Cylinder045,Cylinder047]
FEATURE [Part::Box] Box028  label="Cubo026"
  AttacherType = Attacher::AttachEngine3D
  Height = 2
  Length = 25
  Placement = pos=(-23,0,33) rot=(0,0,1;0rad)
  Width = 10
FEATURE [Part::MultiFuse] Fusion020
  Shapes = -> [Box028,Box027]
FEATURE [Part::Cut] Cut038
  Base = -> Fusion020
  Tool = -> Fusion021
FEATURE [Part::Cut] Cut037
  Base = -> Cut038
  Placement = pos=(121,-20,-29) rot=(0,0,1;0rad)
  Tool = -> Cylinder046
FEATURE [Part::Cut] Cut014  label="separador007"
  Base = -> Prism007
  Placement = pos=(-1,-25,31) rot=(0,0,1;0rad)
  Tool = -> Cylinder033
FEATURE [Part::Prism] Prism016  label="Prisma016"
  AttacherType = Attacher::AttachEngine3D
  Circumradius = 2
  Height = 10
  Placement = pos=(107,-15,4) rot=(0,0,1;0rad)
  Polygon = 6
FEATURE [Part::Cut] Cut039
  Base = -> Cut037
  Tool = -> Prism016
FEATURE [Part::Cylinder] Cylinder048  label="Cilindro048"
  Angle = 360
  AttacherType = Attacher::AttachEngine3D
  Height = 30
  Placement = pos=(0,0,-2) rot=(0,0,1;0rad)
  Radius = 2
FEATURE [Part::Prism] Prism017  label="Prisma017"
  AttacherType = Attacher::AttachEngine3D
  Circumradius = 3.75
  Height = 20
  Polygon = 6
FEATURE [Part::Cut] Cut040  label="separador015"
  Base = -> Prism017
  Placement = pos=(107,-15,4) rot=(0,0,1;0rad)
  Tool = -> Cylinder048
FEATURE [Part::Cut] Cut041
  Base = -> Cut039
  Tool = -> Cut040
FEATURE [Part::Fillet] Fillet010  label="soporteIR2"
  Base = -> Cut041
  Edges = 2 edges r=1.5: [Edge18,Edge29]
FEATURE [Part::Feature] Fillet010_solid001  label="soporteIR2 (Solid)001"
  Placement = pos=(0,30,0) rot=(0,0,1;0rad)
  shape: bbox 25 x 10 x 35 mm, 23 faces (baked)
FEATURE [Part::Feature] nano_expansion_shield001
  shape: bbox 54.3 x 59.3 x 15.08 mm, 16572 faces, 0 solids (baked)
FEATURE [Part::Feature] Fillet010_solid  label="soporteIR2 (Solid)"
  shape: bbox 25 x 10 x 35 mm, 23 faces (baked)
FEATURE [Mesh::Feature] Mesh005  label="soporteIR2 (Solid) (Meshed)"
